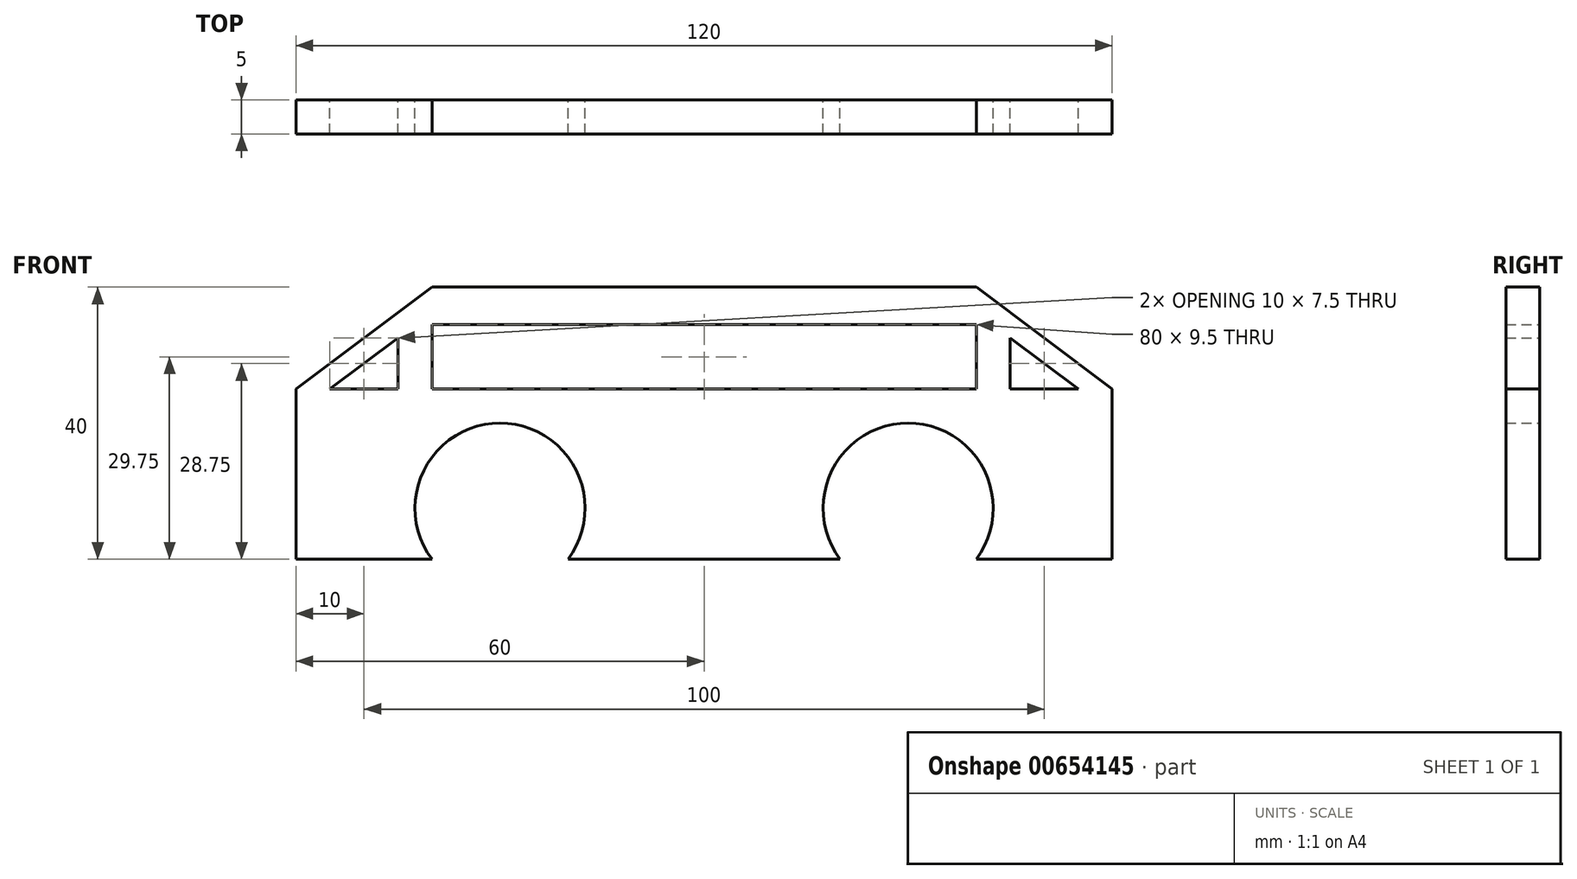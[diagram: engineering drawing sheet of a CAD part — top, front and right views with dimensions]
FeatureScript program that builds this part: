
annotation { "Feature Type Name" : "Feature", "Feature Type Description" : "" }
export const myFeature = defineFeature(function(context is Context, id is Id, definition is map)
    precondition{}
    {
        {
            var Q0;
            Q0=qCreatedBy(makeId("Front.planeOp"),FACE);
            var sketch = newSketch(context, id + "F0", { "sketchPlane" : qUnion([Q0])});
            skLineSegment(sketch, "E0", {"start": v(-60, 0) * mm, "end": v(-42.5, 0) * mm});
            skLineSegment(sketch, "E1", {"start": v(0, 0) * mm, "end": v(17.5, 0) * mm});
            skLineSegment(sketch, "E2", {"start": v(60, 0) * mm, "end": v(60, 25) * mm});
            skLineSegment(sketch, "E3", {"start": v(60, 25) * mm, "end": v(40, 40) * mm});
            skLineSegment(sketch, "E4", {"start": v(40, 40) * mm, "end": v(-40, 40) * mm});
            skLineSegment(sketch, "E5", {"start": v(-40, 40) * mm, "end": v(-60, 25) * mm});
            skLineSegment(sketch, "E6", {"start": v(-60, 25) * mm, "end": v(-60, 0) * mm});
            skLineSegment(sketch, "E7.bottom", {"start": v(-40, 34.5) * mm, "end": v(40, 34.5) * mm});
            skLineSegment(sketch, "E7.top", {"start": v(-40, 25) * mm, "end": v(40, 25) * mm});
            skLineSegment(sketch, "E7.left", {"start": v(-40, 34.5) * mm, "end": v(-40, 25) * mm});
            skLineSegment(sketch, "E7.right", {"start": v(40, 34.5) * mm, "end": v(40, 25) * mm});
            skLineSegment(sketch, "E8", {"start": v(55, 25) * mm, "end": v(45, 25) * mm});
            skLineSegment(sketch, "E9", {"start": v(45, 25) * mm, "end": v(45, 32.5) * mm});
            skLineSegment(sketch, "E10", {"start": v(45, 32.5) * mm, "end": v(55, 25) * mm});
            skLineSegment(sketch, "E11", {"start": v(-45, 25) * mm, "end": v(-55, 25) * mm});
            skLineSegment(sketch, "E12", {"start": v(-55, 25) * mm, "end": v(-45, 32.5) * mm});
            skLineSegment(sketch, "E13", {"start": v(-45, 32.5) * mm, "end": v(-45, 25) * mm});
            skLineSegment(sketch, "E14.trimOffspring", {"start": v(-17.5, 0) * mm, "end": v(0, 0) * mm});
            skLineSegment(sketch, "E15.trimOffspring", {"start": v(42.5, 0) * mm, "end": v(60, 0) * mm});
            skLineSegment(sketch, "E16", {"start": v(-42.5, 0) * mm, "end": v(-40, 0) * mm});
            skLineSegment(sketch, "E17", {"start": v(17.5, 0) * mm, "end": v(20, 0) * mm});
            skArc(sketch, "E18", {"start": v(-20, 0) * mm, "mid": v(-30, 20) * mm, "end": v(-40, 0) * mm});
            skArc(sketch, "E19", {"start": v(40, 0) * mm, "mid": v(30, 20) * mm, "end": v(20, 0) * mm});
            skLineSegment(sketch, "E20.trimOffspring", {"start": v(-20, 0) * mm, "end": v(-17.5, 0) * mm});
            skLineSegment(sketch, "E21.trimOffspring", {"start": v(40, 0) * mm, "end": v(42.5, 0) * mm});
            skSolve(sketch);
        }
        {
            var Q0;
            Q0 = qSketchRegion(id + "F0", true);
            extrude(context, id + "F1", {"entities" : qUnion([Q0]), "depth" : 5 * mm, "offsetDistance" : 25 * mm});
        }
    });
